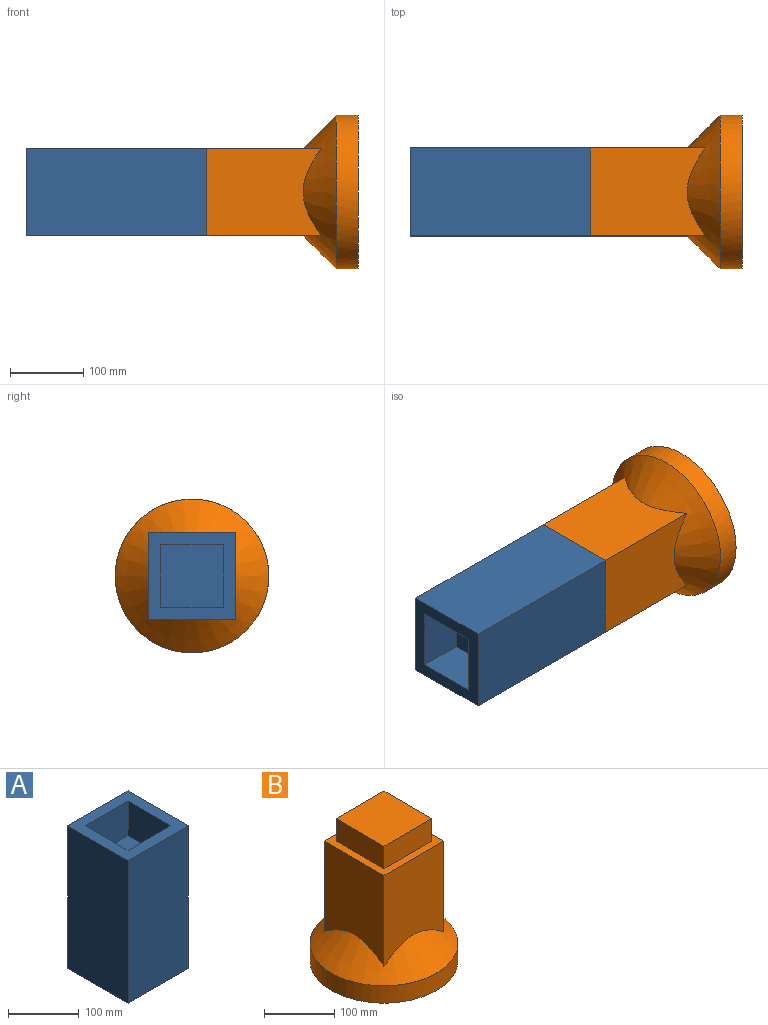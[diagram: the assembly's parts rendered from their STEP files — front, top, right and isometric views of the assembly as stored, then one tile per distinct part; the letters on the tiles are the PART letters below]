
ASSEMBLY  parts=2 mates=1
PART A: 16 faces, bbox 120x120x246 mm
  f0: plane 246x120mm, normal (0,1,0), area 29520mm2, adj f1,f3,f4,f5
  f1: plane 246x120mm, normal (-1,0,0), area 29520mm2, adj f0,f2,f4,f5
  f2: plane 246x120mm, normal (0,-1,0), area 29520mm2, adj f1,f3,f4,f5
  f3: plane 246x120mm, normal (1,0,0), area 29520mm2, adj f0,f2,f4,f5
  f4: plane 120x120mm, normal (0,0,1), area 7175mm2, adj f0,f1,f2,f3,f11,f12,f13,f14
  f5: plane 120x120mm, normal (0,0,-1), area 4400mm2, adj f0,f1,f2,f3,f6,f7,f8,f9
  f6: plane 100x40mm, normal (1,0,0), area 4000mm2, adj f5,f7,f9,f10
  f7: plane 100x40mm, normal (0,-1,0), area 4000mm2, adj f5,f6,f8,f10
  f8: plane 100x40mm, normal (-1,0,0), area 4000mm2, adj f5,f7,f9,f10
  f9: plane 100x40mm, normal (0,1,0), area 4000mm2, adj f5,f6,f8,f10
  f10: plane 100x100mm, normal (0,0,-1), area 10000mm2, adj f6,f7,f8,f9
  f11: plane 85x60mm, normal (1,0,0), area 5100mm2, adj f4,f12,f14,f15
  f12: plane 85x60mm, normal (0,1,0), area 5100mm2, adj f4,f11,f13,f15
  f13: plane 85x60mm, normal (-1,0,0), area 5100mm2, adj f4,f12,f14,f15
  f14: plane 85x60mm, normal (0,-1,0), area 5100mm2, adj f4,f11,f13,f15
  f15: plane 85x85mm, normal (0,0,1), area 7225mm2, adj f11,f12,f13,f14
PART B: 13 faces, bbox 210x210x246.4 mm
  f0: plane 157.23x120mm, normal (0,1,0), area 16949.8mm2, adj f1,f3,f8,f12
  f1: plane 157.23x120mm, normal (-1,0,0), area 16949.7mm2, adj f0,f2,f8,f12
  f2: plane 157.23x120mm, normal (0,-1,0), area 16949.8mm2, adj f1,f3,f8,f12
  f3: plane 157.23x120mm, normal (1,0,0), area 16949.7mm2, adj f0,f2,f8,f12
  f4: plane 96x39mm, normal (0,-1,0), area 3744mm2, adj f5,f7,f8,f9
  f5: plane 96x39mm, normal (-1,0,0), area 3744mm2, adj f4,f6,f8,f9
  f6: plane 96x39mm, normal (0,1,0), area 3744mm2, adj f5,f7,f8,f9
  f7: plane 96x39mm, normal (1,0,0), area 3744mm2, adj f4,f6,f8,f9
  f8: plane 120x120mm, normal (0,0,1), area 5184mm2, adj f0,f1,f2,f3,f4,f5,f6,f7
  f9: plane 96x96mm, normal (0,0,1), area 9216mm2, adj f4,f5,f6,f7
  f10: cylinder r=105mm len=210mm, axis (0,0,-1), area 19792mm2, adj f11,f12
  f11: plane 210x210mm, normal (0,0,-1), area 34636.1mm2, adj f10
  f12: cone r=105mm half-angle=45deg, axis (0,0,-1), area 28617.9mm2, adj f0,f1,f2,f3,f10
PLACE A rot(axis=(0.58,-0.58,-0.58),120deg) t=(-143.83,17.42,-35.02)mm
PLACE B rot(axis=(0.58,-0.58,-0.58),120deg) t=(63.55,17.42,-35.02)mm
MATE fastened B.f8 <-> A.f5  axis (-1,0,0) through (-143.83,17.42,-35.02)mm
